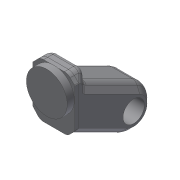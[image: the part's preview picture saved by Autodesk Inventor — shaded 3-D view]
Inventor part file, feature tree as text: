
AUTODESK INVENTOR PART (.ipt)
format: ipt  version: 2018 (Build 220112000, 112)  size: 240,128 bytes
history: native  units: mm
features: other x4, extrude x3, sketch x3, plane x1, imported_body x1, boolean_combine x1, reference x1
ambient origin geometry x8: Origin, YZ Plane, XZ Plane, XY Plane, X Axis, Y Axis, Z Axis, Center Point
bodies: Solid1 (feature_tree), Solid2 (feature_tree)
feature tree (14):
  extrude  "Extrusion1"  Depth=7.0mm TaperAngle=0.0deg
  extrude  "Extrusion2"  Depth=4.0mm TaperAngle=0.0deg
  sketch  "Sketch10"  dims[d44=10.0mm d45=0.0mm]
  plane  "Work Plane1"
  extrude  "Extrusion7"  [1 undecoded]
  imported_body  "Base1"
  boolean_combine  "Combine1"
  sketch  "Sketch1"  dims[d0=40.0mm d1=7.0mm d2=0.0mm]
  sketch  "Sketch2"  dims[d3=80.4mm d4=4.0mm d5=0.0mm]
  reference  "Reference3"
  parser-record x1  (decoder bookkeeping rows leaked as tree rows — omitted from the tree; the rows remain in map.json)
  other  "servocheck.iam"
  other  "bottomarm:1"
  other  "arm1:1"
note: 1 required parameter value undecoded (feature->parameter linkage not recoverable at this tier; creation-order binding heuristic only, values carry confidence <= 0.55)
note: 1 file-system path scrubbed to <path> (originals preserved in map.json)
